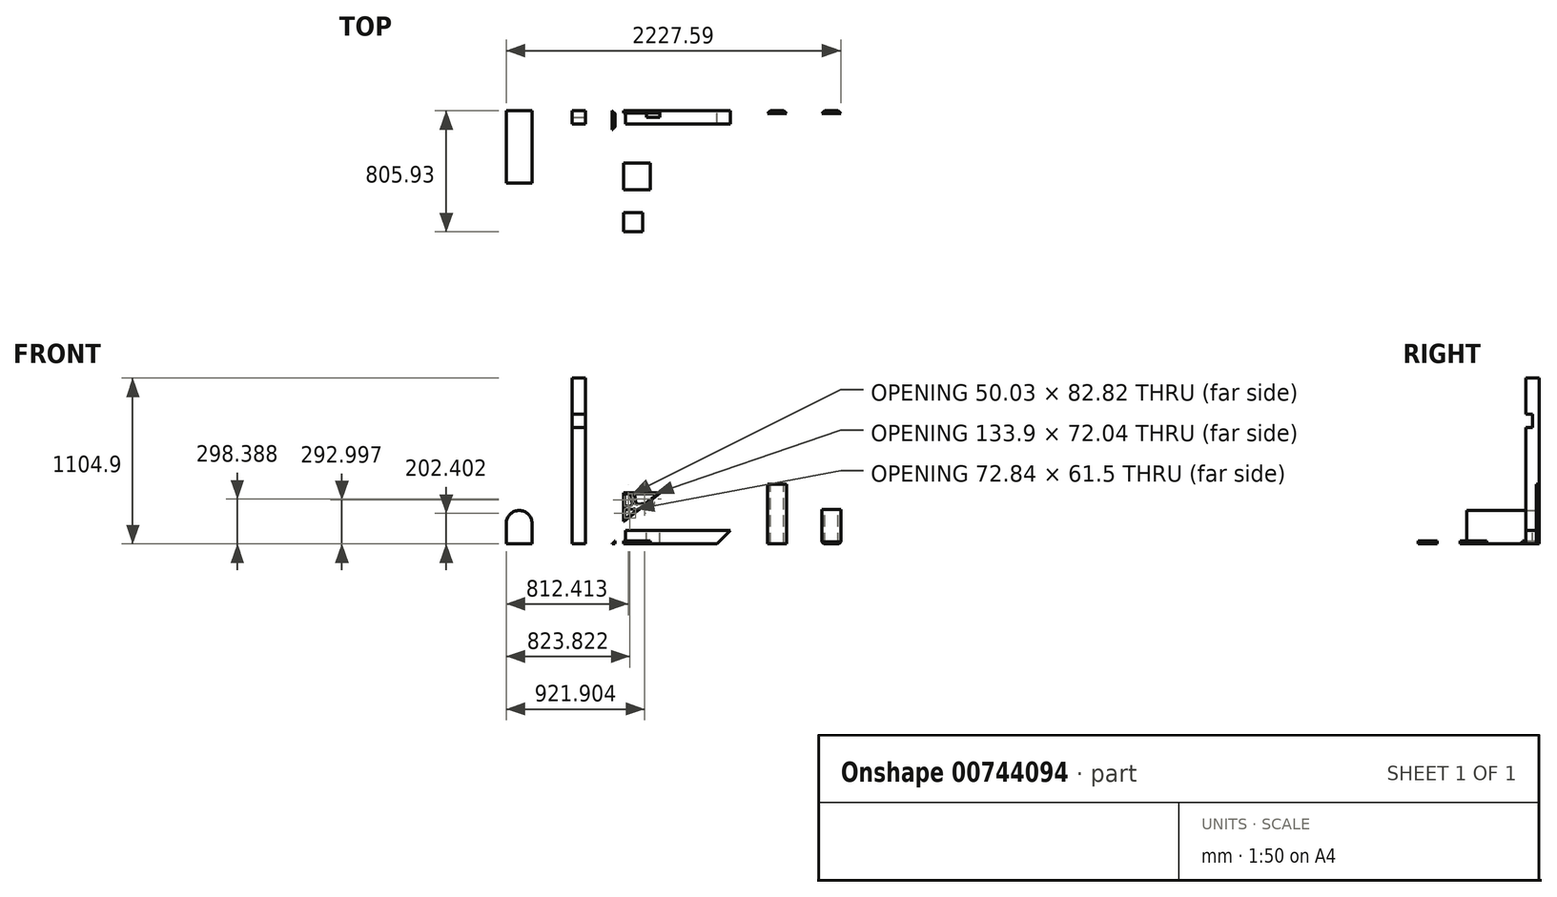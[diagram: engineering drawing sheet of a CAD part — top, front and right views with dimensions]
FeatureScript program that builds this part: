
annotation { "Feature Type Name" : "Feature", "Feature Type Description" : "" }
export const myFeature = defineFeature(function(context is Context, id is Id, definition is map)
    precondition{}
    {
        {
            var Q0;
            Q0=qCreatedBy(makeId("Front.planeOp"),FACE);
            var sketch = newSketch(context, id + "F0", { "sketchPlane" : qUnion([Q0])});
            skLineSegment(sketch, "E0", {"start": v(-781.05, 0) * mm, "end": v(-609.6, 0) * mm});
            skLineSegment(sketch, "E1", {"start": v(-781.05, 0) * mm, "end": v(-781.05, 136.53) * mm});
            skLineSegment(sketch, "E2", {"start": v(-609.6, 0) * mm, "end": v(-609.6, 136.53) * mm});
            skArc(sketch, "E3", {"start": v(-781.05, 136.53) * mm, "mid": v(-695.32, 222.25) * mm, "end": v(-609.6, 136.53) * mm});
            skSolve(sketch);
        }
        {
            var Q0;
            Q0=makeQuery(id+"F0.imprint","IMPRINT",FACE,{"disambiguationData":[TD([[makeQuery(id+"F0.imprint","IMPRINT",EDGE,{"derivedFrom":sQuery(id+"F0.wireOp",EDGE,"E0")}),1.0]])]});
            extrude(context, id + "F1", {"entities" : qUnion([Q0]), "depth" : 482.6 * mm, "offsetDistance" : 25.4 * mm});
        }
        {
            var Q0;
            Q0=qCreatedBy(makeId("Front.planeOp"),FACE);
            var sketch = newSketch(context, id + "F2", { "sketchPlane" : qUnion([Q0])});
            skLineSegment(sketch, "E4.bottom", {"start": v(-342.9, 0) * mm, "end": v(-254, 0) * mm});
            skLineSegment(sketch, "E4.left", {"start": v(-342.9, 0) * mm, "end": v(-342.9, 1104.9) * mm});
            skLineSegment(sketch, "E4.right", {"start": v(-254, 0) * mm, "end": v(-254, 1193.8) * mm});
            skLineSegment(sketch, "E5", {"start": v(-254, 1193.8) * mm, "end": v(-342.9, 1104.9) * mm});
            skSolve(sketch);
        }
        {
            var Q0;
            Q0=makeQuery(id+"F2.imprint","IMPRINT",FACE,{"disambiguationData":[TD([[makeQuery(id+"F2.imprint","IMPRINT",EDGE,{"derivedFrom":sQuery(id+"F2.wireOp",EDGE,"E4.bottom")}),1.0]])]});
            extrude(context, id + "F3", {"entities" : qUnion([Q0]), "depth" : 88.9 * mm, "offsetDistance" : 25.4 * mm});
        }
        {
            var Q0;
            Q0=makeQuery(id+"F3.opExtrude","CAP_FACE",FACE,{"disambiguationData":[OSD([sQuery(id+"F2.wireOp",EDGE,"E4.bottom"),sQuery(id+"F2.wireOp",EDGE,"E4.left"),sQuery(id+"F2.wireOp",EDGE,"E4.right"),sQuery(id+"F2.wireOp",EDGE,"E5")])],"isStart":false});
            var sketch = newSketch(context, id + "F4", { "sketchPlane" : qUnion([Q0])});
            skLineSegment(sketch, "E6.bottom", {"start": v(-342.9, 863.6) * mm, "end": v(-254, 863.6) * mm});
            skLineSegment(sketch, "E6.top", {"start": v(-342.9, 774.7) * mm, "end": v(-254, 774.7) * mm});
            skLineSegment(sketch, "E6.left", {"start": v(-342.9, 863.6) * mm, "end": v(-342.9, 774.7) * mm});
            skLineSegment(sketch, "E6.right", {"start": v(-254, 863.6) * mm, "end": v(-254, 774.7) * mm});
            skSolve(sketch);
        }
        {
            var Q0;
            Q0=makeQuery(id+"F4.imprint","IMPRINT",FACE,{"disambiguationData":[TD([[makeQuery(id+"F4.imprint","IMPRINT",EDGE,{"derivedFrom":sQuery(id+"F4.wireOp",EDGE,"E6.bottom")}),-1.0]])]});
            extrude(context, id + "F5", {"entities" : qUnion([Q0]), "operationType" : NewBodyOperationType.REMOVE, "oppositeDirection" : true, "depth" : 44.45 * mm, "offsetDistance" : 25.4 * mm});
        }
        {
            var Q0;
            Q0=qCreatedBy(makeId("Front.planeOp"),FACE);
            var sketch = newSketch(context, id + "F6", { "sketchPlane" : qUnion([Q0])});
            skLineSegment(sketch, "E7.bottom", {"start": v(-76.2, 0) * mm, "end": v(622.3, 0) * mm});
            skLineSegment(sketch, "E7.top", {"start": v(12.7, 88.9) * mm, "end": v(711.2, 88.9) * mm});
            skLineSegment(sketch, "E8", {"start": v(711.2, 88.9) * mm, "end": v(622.3, 0) * mm});
            skLineSegment(sketch, "E9", {"start": v(-76.2, 0) * mm, "end": v(12.7, 88.9) * mm});
            skSolve(sketch);
        }
        {
            var Q0;
            Q0=makeQuery(id+"F6.imprint","IMPRINT",FACE,{"disambiguationData":[TD([[makeQuery(id+"F6.imprint","IMPRINT",EDGE,{"derivedFrom":sQuery(id+"F6.wireOp",EDGE,"E7.bottom")}),1.0]])]});
            extrude(context, id + "F7", {"entities" : qUnion([Q0]), "depth" : 88.9 * mm, "offsetDistance" : 25.4 * mm});
        }
        {
            var Q0;
            Q0=makeQuery(id+"F7.opExtrude","CAP_FACE",FACE,{"disambiguationData":[OSD([sQuery(id+"F6.wireOp",EDGE,"E7.bottom"),sQuery(id+"F6.wireOp",EDGE,"E7.top"),sQuery(id+"F6.wireOp",EDGE,"E8"),sQuery(id+"F6.wireOp",EDGE,"E9")])],"isStart":true});
            var sketch = newSketch(context, id + "F8", { "sketchPlane" : qUnion([Q0])});
            skLineSegment(sketch, "E10.bottom", {"start": v(-152.4, 0) * mm, "end": v(-241.3, 0) * mm});
            skLineSegment(sketch, "E10.top", {"start": v(-152.4, 88.9) * mm, "end": v(-241.3, 88.9) * mm});
            skLineSegment(sketch, "E10.left", {"start": v(-152.4, 0) * mm, "end": v(-152.4, 88.9) * mm});
            skLineSegment(sketch, "E10.right", {"start": v(-241.3, 0) * mm, "end": v(-241.3, 88.9) * mm});
            skSolve(sketch);
        }
        {
            var Q0;
            Q0=makeQuery(id+"F8.imprint","IMPRINT",FACE,{"disambiguationData":[TD([[makeQuery(id+"F8.imprint","IMPRINT",EDGE,{"derivedFrom":sQuery(id+"F8.wireOp",EDGE,"E10.bottom")}),-1.0]])]});
            extrude(context, id + "F9", {"entities" : qUnion([Q0]), "operationType" : NewBodyOperationType.REMOVE, "oppositeDirection" : true, "depth" : 44.45 * mm, "offsetDistance" : 25.4 * mm});
        }
        {
            var Q0;
            Q0=qCreatedBy(makeId("Front.planeOp"),FACE);
            var sketch = newSketch(context, id + "F10", { "sketchPlane" : qUnion([Q0])});
            skLineSegment(sketch, "E11.bottom", {"start": v(889.1, 0) * mm, "end": v(1232, 0) * mm});
            skLineSegment(sketch, "E11.top", {"start": v(978, 88.9) * mm, "end": v(1143.1, 88.9) * mm});
            skLineSegment(sketch, "E12", {"start": v(1232, 0) * mm, "end": v(1143.1, 88.9) * mm});
            skLineSegment(sketch, "E13", {"start": v(889.1, 0) * mm, "end": v(978, 88.9) * mm});
            skSolve(sketch);
        }
        {
            var Q0;
            Q0=makeQuery(id+"F10.imprint","IMPRINT",FACE,{"disambiguationData":[TD([[makeQuery(id+"F10.imprint","IMPRINT",EDGE,{"derivedFrom":sQuery(id+"F10.wireOp",EDGE,"E11.bottom")}),1.0]])]});
            extrude(context, id + "F11", {"entities" : qUnion([Q0]), "depth" : 88.9 * mm, "offsetDistance" : 25.4 * mm});
        }
        {
            var Q0;
            {var subQ0=sQuery(id+"F2.wireOp",EDGE,"E4.left");var subQ1=sQuery(id+"F2.wireOp",EDGE,"E4.right");var subQ2=sQuery(id+"F2.wireOp",EDGE,"E5");Q0=makeQuery(id+"F5.boolean.opBoolean","SPLIT",FACE,{"disambiguationData":[TD([makeQuery(id+"F3.opExtrude","SWEPT_FACE",FACE,{"disambiguationData":[OSD([subQ2])]})])],"derivedFrom":makeQuery(id+"F3.opExtrude","CAP_FACE",FACE,{"disambiguationData":[OSD([sQuery(id+"F2.wireOp",EDGE,"E4.bottom"),subQ0,subQ1,subQ2])],"isStart":false})});}
            var sketch = newSketch(context, id + "F12", { "sketchPlane" : qUnion([Q0])});
            skLineSegment(sketch, "E14.bottom", {"start": v(-342.9, 1104.9) * mm, "end": v(-254, 1104.9) * mm});
            skLineSegment(sketch, "E14.top", {"start": v(-342.9, 1200.15) * mm, "end": v(-254, 1200.15) * mm});
            skLineSegment(sketch, "E14.left", {"start": v(-342.9, 1104.9) * mm, "end": v(-342.9, 1200.15) * mm});
            skLineSegment(sketch, "E14.right", {"start": v(-254, 1104.9) * mm, "end": v(-254, 1200.15) * mm});
            skSolve(sketch);
        }
        {
            var Q0;
            Q0 = qSketchRegion(id + "F12", true);
            extrude(context, id + "F13", {"entities" : qUnion([Q0]), "operationType" : NewBodyOperationType.REMOVE, "oppositeDirection" : true, "depth" : 88.9 * mm, "offsetDistance" : 25.4 * mm});
        }
        {
            var Q0;
            Q0=makeQuery(id+"F7.opExtrude","CAP_FACE",FACE,{"disambiguationData":[OSD([sQuery(id+"F6.wireOp",EDGE,"E7.bottom"),sQuery(id+"F6.wireOp",EDGE,"E7.top"),sQuery(id+"F6.wireOp",EDGE,"E8"),sQuery(id+"F6.wireOp",EDGE,"E9")])],"isStart":false});
            var sketch = newSketch(context, id + "F14", { "sketchPlane" : qUnion([Q0])});
            skLineSegment(sketch, "E15.bottom", {"start": v(12.7, 88.9) * mm, "end": v(-82.55, 88.9) * mm});
            skLineSegment(sketch, "E15.top", {"start": v(12.7, 0) * mm, "end": v(-82.55, 0) * mm});
            skLineSegment(sketch, "E15.left", {"start": v(12.7, 88.9) * mm, "end": v(12.7, 0) * mm});
            skLineSegment(sketch, "E15.right", {"start": v(-82.55, 88.9) * mm, "end": v(-82.55, 0) * mm});
            skSolve(sketch);
        }
        {
            var Q0;
            Q0=makeQuery(id+"F14.imprint","IMPRINT",FACE,{"disambiguationData":[TD([[makeQuery(id+"F14.imprint","IMPRINT",EDGE,{"derivedFrom":sQuery(id+"F14.wireOp",EDGE,"E15.bottom")}),1.0]])]});
            var Q1;
            {var subQ2=sQuery(id+"F14.wireOp",EDGE,"E15.left");Q1=makeQuery(id+"F14.imprint","IMPRINT",FACE,{"disambiguationData":[TD([[makeQuery(id+"F14.imprint","IMPRINT",EDGE,{"derivedFrom":subQ2}),-1.0]])]});}
            extrude(context, id + "F15", {"entities" : qUnion([Q0, Q1]), "operationType" : NewBodyOperationType.REMOVE, "oppositeDirection" : true, "depth" : 88.9 * mm, "offsetDistance" : 25.4 * mm});
        }
        {
            var Q0;
            Q0=makeQuery(id+"F11.opExtrude","SWEPT_BODY",BODY,{"disambiguationData":[OSD([sQuery(id+"F10.wireOp",EDGE,"E11.bottom"),sQuery(id+"F10.wireOp",EDGE,"E11.top"),sQuery(id+"F10.wireOp",EDGE,"E12"),sQuery(id+"F10.wireOp",EDGE,"E13")])]});
            deleteBodies(context, id + "F16", {"entities" : qUnion([Q0])});
        }
        {
            var Q0;
            Q0=qCreatedBy(makeId("Front.planeOp"),FACE);
            var sketch = newSketch(context, id + "F17", { "sketchPlane" : qUnion([Q0])});
            skLineSegment(sketch, "E16.bottom", {"start": v(959.17, 0) * mm, "end": v(1086.17, 0) * mm});
            skLineSegment(sketch, "E16.top", {"start": v(959.17, 396.88) * mm, "end": v(1086.17, 396.88) * mm});
            skLineSegment(sketch, "E16.left", {"start": v(959.17, 0) * mm, "end": v(959.17, 396.88) * mm});
            skLineSegment(sketch, "E16.right", {"start": v(1086.17, 0) * mm, "end": v(1086.17, 396.88) * mm});
            skSolve(sketch);
        }
        {
            var Q0;
            Q0=makeQuery(id+"F17.imprint","IMPRINT",FACE,{"disambiguationData":[TD([[makeQuery(id+"F17.imprint","IMPRINT",EDGE,{"derivedFrom":sQuery(id+"F17.wireOp",EDGE,"E16.bottom")}),1.0]])]});
            extrude(context, id + "F18", {"entities" : qUnion([Q0]), "depth" : 19.05 * mm, "offsetDistance" : 25.4 * mm});
        }
        {
            var Q0;
            Q0=makeQuery(id+"F18.opExtrude","SWEPT_FACE",FACE,{"disambiguationData":[OSD([sQuery(id+"F17.wireOp",EDGE,"E16.top")])]});
            var sketch = newSketch(context, id + "F19", { "sketchPlane" : qUnion([Q0])});
            skLineSegment(sketch, "E17", {"start": v(959.17, -19.05) * mm, "end": v(978.22, 0) * mm});
            skLineSegment(sketch, "E18", {"start": v(1086.17, -19.05) * mm, "end": v(1067.12, 0) * mm});
            skLineSegment(sketch, "E19", {"start": v(978.22, 0) * mm, "end": v(959.17, 0) * mm});
            skLineSegment(sketch, "E20", {"start": v(959.17, 0) * mm, "end": v(959.17, -19.05) * mm});
            skLineSegment(sketch, "E21", {"start": v(1067.12, 0) * mm, "end": v(1086.17, 0) * mm});
            skLineSegment(sketch, "E22", {"start": v(1086.17, 0) * mm, "end": v(1086.17, -19.05) * mm});
            skSolve(sketch);
        }
        {
            var Q0;
            Q0=makeQuery(id+"F19.imprint","IMPRINT",FACE,{"disambiguationData":[TD([[makeQuery(id+"F19.imprint","IMPRINT",EDGE,{"derivedFrom":sQuery(id+"F19.wireOp",EDGE,"E17")}),1.0]])]});
            var Q1;
            Q1=makeQuery(id+"F19.imprint","IMPRINT",FACE,{"disambiguationData":[TD([[makeQuery(id+"F19.imprint","IMPRINT",EDGE,{"derivedFrom":sQuery(id+"F19.wireOp",EDGE,"E18")}),-1.0]])]});
            extrude(context, id + "F20", {"entities" : qUnion([Q0, Q1]), "operationType" : NewBodyOperationType.REMOVE, "endBound" : BoundingType.THROUGH_ALL, "oppositeDirection" : true, "depth" : 25.4 * mm, "offsetDistance" : 25.4 * mm});
        }
        {
            var Q0;
            Q0=qCreatedBy(makeId("Front.planeOp"),FACE);
            var sketch = newSketch(context, id + "F21", { "sketchPlane" : qUnion([Q0])});
            skLineSegment(sketch, "E23.bottom", {"start": v(1319.54, 0) * mm, "end": v(1446.54, 0) * mm});
            skLineSegment(sketch, "E23.top", {"start": v(1319.54, 228.6) * mm, "end": v(1446.54, 228.6) * mm});
            skLineSegment(sketch, "E23.left", {"start": v(1319.54, 0) * mm, "end": v(1319.54, 228.6) * mm});
            skLineSegment(sketch, "E23.right", {"start": v(1446.54, 0) * mm, "end": v(1446.54, 228.6) * mm});
            skSolve(sketch);
        }
        {
            var Q0;
            Q0=makeQuery(id+"F21.imprint","IMPRINT",FACE,{"disambiguationData":[TD([[makeQuery(id+"F21.imprint","IMPRINT",EDGE,{"derivedFrom":sQuery(id+"F21.wireOp",EDGE,"E23.bottom")}),1.0]])]});
            extrude(context, id + "F22", {"entities" : qUnion([Q0]), "depth" : 19.05 * mm, "offsetDistance" : 25.4 * mm});
        }
        {
            var Q0;
            Q0=makeQuery(id+"F22.opExtrude","SWEPT_FACE",FACE,{"disambiguationData":[OSD([sQuery(id+"F21.wireOp",EDGE,"E23.top")])]});
            var sketch = newSketch(context, id + "F23", { "sketchPlane" : qUnion([Q0])});
            skLineSegment(sketch, "E24", {"start": v(1319.54, -19.05) * mm, "end": v(1338.6, 0) * mm});
            skLineSegment(sketch, "E25", {"start": v(1338.6, 0) * mm, "end": v(1319.54, 0) * mm});
            skLineSegment(sketch, "E26", {"start": v(1319.54, 0) * mm, "end": v(1319.54, -19.05) * mm});
            skLineSegment(sketch, "E27", {"start": v(1446.54, -19.05) * mm, "end": v(1427.5, 0) * mm});
            skLineSegment(sketch, "E28", {"start": v(1427.5, 0) * mm, "end": v(1446.54, 0) * mm});
            skLineSegment(sketch, "E29", {"start": v(1446.54, 0) * mm, "end": v(1446.54, -19.05) * mm});
            skSolve(sketch);
        }
        {
            var Q0;
            Q0=makeQuery(id+"F23.imprint","IMPRINT",FACE,{"disambiguationData":[TD([[makeQuery(id+"F23.imprint","IMPRINT",EDGE,{"derivedFrom":sQuery(id+"F23.wireOp",EDGE,"E27")}),-1.0]])]});
            var Q1;
            Q1=makeQuery(id+"F23.imprint","IMPRINT",FACE,{"disambiguationData":[TD([[makeQuery(id+"F23.imprint","IMPRINT",EDGE,{"derivedFrom":sQuery(id+"F23.wireOp",EDGE,"E24")}),1.0]])]});
            extrude(context, id + "F24", {"entities" : qUnion([Q0, Q1]), "operationType" : NewBodyOperationType.REMOVE, "endBound" : BoundingType.THROUGH_ALL, "oppositeDirection" : true, "depth" : 25.4 * mm, "offsetDistance" : 25.4 * mm});
        }
        {
            var Q0;
            Q0=qCreatedBy(makeId("Front.planeOp"),FACE);
            var sketch = newSketch(context, id + "F25", { "sketchPlane" : qUnion([Q0])});
            skLineSegment(sketch, "E30.bottom", {"start": v(-57.23, 0) * mm, "end": v(-76.28, 0) * mm});
            skLineSegment(sketch, "E30.top", {"start": v(-57.23, 19.05) * mm, "end": v(-60.4, 19.05) * mm});
            skLineSegment(sketch, "E30.left", {"start": v(-57.23, 0) * mm, "end": v(-57.23, 19.05) * mm});
            skLineSegment(sketch, "E30.right", {"start": v(-76.28, 0) * mm, "end": v(-76.28, 3.18) * mm});
            skArc(sketch, "E31", {"start": v(-76.28, 3.18) * mm, "mid": v(-65.06, 7.82) * mm, "end": v(-60.4, 19.05) * mm});
            skSolve(sketch);
        }
        {
            var Q0;
            Q0=makeQuery(id+"F25.imprint","IMPRINT",FACE,{"disambiguationData":[TD([[makeQuery(id+"F25.imprint","IMPRINT",EDGE,{"derivedFrom":sQuery(id+"F25.wireOp",EDGE,"E30.bottom")}),-1.0]])]});
            extrude(context, id + "F26", {"entities" : qUnion([Q0]), "depth" : 127 * mm, "offsetDistance" : 25.4 * mm});
        }
        {
            var Q0;
            Q0=makeQuery(id+"F26.opExtrude","SWEPT_FACE",FACE,{"disambiguationData":[OSD([sQuery(id+"F25.wireOp",EDGE,"E30.bottom")])]});
            var sketch = newSketch(context, id + "F27", { "sketchPlane" : qUnion([Q0])});
            skLineSegment(sketch, "E32", {"start": v(-76.28, 0) * mm, "end": v(-57.23, 19.05) * mm});
            skLineSegment(sketch, "E33", {"start": v(-76.28, 127) * mm, "end": v(-57.23, 107.95) * mm});
            skLineSegment(sketch, "E34", {"start": v(-57.23, 107.95) * mm, "end": v(-57.23, 127) * mm});
            skLineSegment(sketch, "E35", {"start": v(-57.23, 127) * mm, "end": v(-76.28, 127) * mm});
            skLineSegment(sketch, "E36", {"start": v(-76.28, 0) * mm, "end": v(-57.23, 0) * mm});
            skLineSegment(sketch, "E37", {"start": v(-57.23, 0) * mm, "end": v(-57.23, 19.05) * mm});
            skSolve(sketch);
        }
        {
            var Q0;
            Q0=makeQuery(id+"F27.imprint","IMPRINT",FACE,{"disambiguationData":[TD([[makeQuery(id+"F27.imprint","IMPRINT",EDGE,{"derivedFrom":sQuery(id+"F27.wireOp",EDGE,"E32")}),-1.0]])]});
            var Q1;
            Q1=makeQuery(id+"F27.imprint","IMPRINT",FACE,{"disambiguationData":[TD([[makeQuery(id+"F27.imprint","IMPRINT",EDGE,{"derivedFrom":sQuery(id+"F27.wireOp",EDGE,"E33")}),1.0]])]});
            extrude(context, id + "F28", {"entities" : qUnion([Q0, Q1]), "operationType" : NewBodyOperationType.REMOVE, "endBound" : BoundingType.THROUGH_ALL, "oppositeDirection" : true, "depth" : 25.4 * mm, "offsetDistance" : 25.4 * mm});
        }
        {
            var Q0;
            Q0=qCreatedBy(makeId("Top.planeOp"),FACE);
            var sketch = newSketch(context, id + "F29", { "sketchPlane" : qUnion([Q0])});
            skLineSegment(sketch, "E38.bottom", {"start": v(0, -525.83) * mm, "end": v(177.8, -525.83) * mm});
            skLineSegment(sketch, "E38.top", {"start": v(0, -348.03) * mm, "end": v(177.8, -348.03) * mm});
            skLineSegment(sketch, "E38.left", {"start": v(0, -525.83) * mm, "end": v(0, -348.03) * mm});
            skLineSegment(sketch, "E38.right", {"start": v(177.8, -525.83) * mm, "end": v(177.8, -348.03) * mm});
            skSolve(sketch);
        }
        {
            var Q0;
            Q0=makeQuery(id+"F29.imprint","IMPRINT",FACE,{"disambiguationData":[TD([[makeQuery(id+"F29.imprint","IMPRINT",EDGE,{"derivedFrom":sQuery(id+"F29.wireOp",EDGE,"E38.bottom")}),1.0]])]});
            extrude(context, id + "F30", {"entities" : qUnion([Q0]), "depth" : 19.05 * mm, "offsetDistance" : 25.4 * mm});
        }
        {
            var Q0;
            Q0=qCreatedBy(makeId("Top.planeOp"),FACE);
            var sketch = newSketch(context, id + "F31", { "sketchPlane" : qUnion([Q0])});
            skLineSegment(sketch, "E39.bottom", {"start": v(0, -805.93) * mm, "end": v(127, -805.93) * mm});
            skLineSegment(sketch, "E39.top", {"start": v(0, -678.93) * mm, "end": v(127, -678.93) * mm});
            skLineSegment(sketch, "E39.left", {"start": v(0, -805.93) * mm, "end": v(0, -678.93) * mm});
            skLineSegment(sketch, "E39.right", {"start": v(127, -805.93) * mm, "end": v(127, -678.93) * mm});
            skSolve(sketch);
        }
        {
            var Q0;
            Q0=makeQuery(id+"F31.imprint","IMPRINT",FACE,{"disambiguationData":[TD([[makeQuery(id+"F31.imprint","IMPRINT",EDGE,{"derivedFrom":sQuery(id+"F31.wireOp",EDGE,"E39.bottom")}),1.0]])]});
            extrude(context, id + "F32", {"entities" : qUnion([Q0]), "depth" : 19.05 * mm, "offsetDistance" : 25.4 * mm});
        }
        {
            var Q0;
            Q0=qCreatedBy(makeId("Front.planeOp"),FACE);
            var sketch = newSketch(context, id + "F33", { "sketchPlane" : qUnion([Q0])});
            skLineSegment(sketch, "E40.bottom", {"start": v(0, 150.26) * mm, "end": v(241.3, 150.26) * mm});
            skLineSegment(sketch, "E40.top", {"start": v(0, 340.76) * mm, "end": v(241.3, 340.76) * mm});
            skLineSegment(sketch, "E40.left", {"start": v(0, 150.26) * mm, "end": v(0, 340.76) * mm});
            skLineSegment(sketch, "E40.right", {"start": v(241.3, 150.26) * mm, "end": v(241.3, 340.76) * mm});
            skSolve(sketch);
        }
        {
            var Q0;
            Q0=makeQuery(id+"F33.imprint","IMPRINT",FACE,{"disambiguationData":[TD([[makeQuery(id+"F33.imprint","IMPRINT",EDGE,{"derivedFrom":sQuery(id+"F33.wireOp",EDGE,"E40.bottom")}),1.0]])]});
            extrude(context, id + "F34", {"entities" : qUnion([Q0]), "depth" : 15.88 * mm, "offsetDistance" : 25.4 * mm});
        }
        {
            var Q0;
            Q0=makeQuery(id+"F34.opExtrude","CAP_FACE",FACE,{"disambiguationData":[OSD([sQuery(id+"F33.wireOp",EDGE,"E40.bottom"),sQuery(id+"F33.wireOp",EDGE,"E40.top"),sQuery(id+"F33.wireOp",EDGE,"E40.left"),sQuery(id+"F33.wireOp",EDGE,"E40.right")])],"isStart":false});
            var sketch = newSketch(context, id + "F35", { "sketchPlane" : qUnion([Q0])});
            skLineSegment(sketch, "E41", {"start": v(3.17, 337.58) * mm, "end": v(3.18, 150.26) * mm, "construction": true});
            skLineSegment(sketch, "E42", {"start": v(3.17, 337.58) * mm, "end": v(241.3, 337.58) * mm, "construction": true});
            skLineSegment(sketch, "E43", {"start": v(3.17, 150.26) * mm, "end": v(241.3, 337.58) * mm});
            skLineSegment(sketch, "E44", {"start": v(241.3, 337.58) * mm, "end": v(241.3, 150.26) * mm});
            skLineSegment(sketch, "E45", {"start": v(241.3, 150.26) * mm, "end": v(3.17, 150.26) * mm});
            skSolve(sketch);
        }
        {
            var Q0;
            Q0=makeQuery(id+"F35.imprint","IMPRINT",FACE,{"disambiguationData":[TD([[makeQuery(id+"F35.imprint","IMPRINT",EDGE,{"derivedFrom":sQuery(id+"F35.wireOp",EDGE,"E43")}),-1.0]])]});
            extrude(context, id + "F36", {"entities" : qUnion([Q0]), "operationType" : NewBodyOperationType.REMOVE, "endBound" : BoundingType.THROUGH_ALL, "oppositeDirection" : true, "depth" : 25.4 * mm, "offsetDistance" : 25.4 * mm});
        }
        {
            var Q0;
            Q0=makeQuery(id+"F34.opExtrude","CAP_FACE",FACE,{"disambiguationData":[OSD([sQuery(id+"F33.wireOp",EDGE,"E40.bottom"),sQuery(id+"F33.wireOp",EDGE,"E40.top"),sQuery(id+"F33.wireOp",EDGE,"E40.left"),sQuery(id+"F33.wireOp",EDGE,"E40.right")])],"isStart":false});
            var sketch = newSketch(context, id + "F37", { "sketchPlane" : qUnion([Q0])});
            skLineSegment(sketch, "E46.0", {"start": v(6.35, 160.83) * mm, "end": v(6.35, 224.33) * mm});
            skLineSegment(sketch, "E46.1", {"start": v(6.35, 160.83) * mm, "end": v(105.15, 238.55) * mm});
            skLineSegment(sketch, "E46.2", {"start": v(6.35, 334.4) * mm, "end": v(46.65, 334.4) * mm});
            skLineSegment(sketch, "E47", {"start": v(6.35, 224.33) * mm, "end": v(105.15, 238.55) * mm});
            skLineSegment(sketch, "E48", {"start": v(6.35, 250) * mm, "end": v(57.74, 257.4) * mm});
            skLineSegment(sketch, "E49", {"start": v(82.88, 261.01) * mm, "end": v(72.31, 334.4) * mm});
            skLineSegment(sketch, "E50", {"start": v(57.74, 257.4) * mm, "end": v(46.65, 334.4) * mm});
            skLineSegment(sketch, "E51.trimOffspring", {"start": v(72.31, 334.4) * mm, "end": v(227, 334.4) * mm});
            skLineSegment(sketch, "E52.trimOffspring", {"start": v(82.88, 261.01) * mm, "end": v(145.07, 269.96) * mm});
            skLineSegment(sketch, "E53.trimOffspring", {"start": v(145.07, 269.96) * mm, "end": v(227, 334.4) * mm});
            skLineSegment(sketch, "E54.trimOffspring", {"start": v(6.35, 250) * mm, "end": v(6.35, 334.4) * mm});
            skSolve(sketch);
        }
        {
            var Q0;
            Q0=makeQuery(id+"F37.imprint","IMPRINT",FACE,{"disambiguationData":[TD([[makeQuery(id+"F37.imprint","IMPRINT",EDGE,{"derivedFrom":sQuery(id+"F37.wireOp",EDGE,"E46.0")}),-1.0]])]});
            var Q1;
            Q1=makeQuery(id+"F37.imprint","IMPRINT",FACE,{"disambiguationData":[TD([[makeQuery(id+"F37.imprint","IMPRINT",EDGE,{"derivedFrom":sQuery(id+"F37.wireOp",EDGE,"E46.2")}),-1.0]])]});
            var Q2;
            Q2=makeQuery(id+"F37.imprint","IMPRINT",FACE,{"disambiguationData":[TD([[makeQuery(id+"F37.imprint","IMPRINT",EDGE,{"derivedFrom":sQuery(id+"F37.wireOp",EDGE,"E49")}),-1.0]])]});
            extrude(context, id + "F38", {"entities" : qUnion([Q0, Q1, Q2]), "operationType" : NewBodyOperationType.REMOVE, "endBound" : BoundingType.THROUGH_ALL, "oppositeDirection" : true, "depth" : 25.4 * mm, "offsetDistance" : 25.4 * mm});
        }
        {
            var Q0;
            Q0=makeQuery(id+"F38.boolean.opBoolean","COPY",EDGE,{"derivedFrom":makeQuery(id+"F38.opExtrude","SWEPT_EDGE",EDGE,{"disambiguationData":[OSD([sQuery(id+"F37.wireOp",EDGE,"E52.trimOffspring"),sQuery(id+"F37.wireOp",EDGE,"E53.trimOffspring")])]})});
            var Q1;
            Q1=makeQuery(id+"F38.boolean.opBoolean","COPY",EDGE,{"derivedFrom":makeQuery(id+"F38.opExtrude","SWEPT_EDGE",EDGE,{"disambiguationData":[OSD([sQuery(id+"F37.wireOp",EDGE,"E49"),sQuery(id+"F37.wireOp",EDGE,"E52.trimOffspring")])]})});
            var Q2;
            Q2=makeQuery(id+"F38.boolean.opBoolean","COPY",EDGE,{"derivedFrom":makeQuery(id+"F38.opExtrude","SWEPT_EDGE",EDGE,{"disambiguationData":[OSD([sQuery(id+"F37.wireOp",EDGE,"E49"),sQuery(id+"F37.wireOp",EDGE,"E51.trimOffspring")])]})});
            var Q3;
            Q3=makeQuery(id+"F38.boolean.opBoolean","COPY",EDGE,{"derivedFrom":makeQuery(id+"F38.opExtrude","SWEPT_EDGE",EDGE,{"disambiguationData":[OSD([sQuery(id+"F37.wireOp",EDGE,"E51.trimOffspring"),sQuery(id+"F37.wireOp",EDGE,"E53.trimOffspring")])]})});
            var Q4;
            Q4=makeQuery(id+"F38.boolean.opBoolean","COPY",EDGE,{"derivedFrom":makeQuery(id+"F38.opExtrude","SWEPT_EDGE",EDGE,{"disambiguationData":[OSD([sQuery(id+"F37.wireOp",EDGE,"E46.2"),sQuery(id+"F37.wireOp",EDGE,"E50")])]})});
            var Q5;
            Q5=makeQuery(id+"F38.boolean.opBoolean","COPY",EDGE,{"derivedFrom":makeQuery(id+"F38.opExtrude","SWEPT_EDGE",EDGE,{"disambiguationData":[OSD([sQuery(id+"F37.wireOp",EDGE,"E46.2"),sQuery(id+"F37.wireOp",EDGE,"E54.trimOffspring")])]})});
            var Q6;
            Q6=makeQuery(id+"F38.boolean.opBoolean","COPY",EDGE,{"derivedFrom":makeQuery(id+"F38.opExtrude","SWEPT_EDGE",EDGE,{"disambiguationData":[OSD([sQuery(id+"F37.wireOp",EDGE,"E48"),sQuery(id+"F37.wireOp",EDGE,"E54.trimOffspring")])]})});
            var Q7;
            Q7=makeQuery(id+"F38.boolean.opBoolean","COPY",EDGE,{"derivedFrom":makeQuery(id+"F38.opExtrude","SWEPT_EDGE",EDGE,{"disambiguationData":[OSD([sQuery(id+"F37.wireOp",EDGE,"E48"),sQuery(id+"F37.wireOp",EDGE,"E50")])]})});
            var Q8;
            Q8=makeQuery(id+"F38.boolean.opBoolean","COPY",EDGE,{"derivedFrom":makeQuery(id+"F38.opExtrude","SWEPT_EDGE",EDGE,{"disambiguationData":[OSD([sQuery(id+"F37.wireOp",EDGE,"E46.1"),sQuery(id+"F37.wireOp",EDGE,"E47")])]})});
            var Q9;
            Q9=makeQuery(id+"F38.boolean.opBoolean","COPY",EDGE,{"derivedFrom":makeQuery(id+"F38.opExtrude","SWEPT_EDGE",EDGE,{"disambiguationData":[OSD([sQuery(id+"F37.wireOp",EDGE,"E46.0"),sQuery(id+"F37.wireOp",EDGE,"E47")])]})});
            var Q10;
            Q10=makeQuery(id+"F38.boolean.opBoolean","COPY",EDGE,{"derivedFrom":makeQuery(id+"F38.opExtrude","SWEPT_EDGE",EDGE,{"disambiguationData":[OSD([sQuery(id+"F37.wireOp",EDGE,"E46.0"),sQuery(id+"F37.wireOp",EDGE,"E46.1")])]})});
            fillet(context, id + "F39", {"entities" : qUnion([Q0, Q1, Q2, Q3, Q4, Q5, Q6, Q7, Q8, Q9, Q10]), "radius" : 10.16 * mm, "tangentPropagation" : true, "allowEdgeOverflow" : false});
        }
        {
            var Q0;
            Q0=makeQuery(id+"F22.opExtrude","CAP_EDGE",EDGE,{"disambiguationData":[OSD([sQuery(id+"F21.wireOp",EDGE,"E23.bottom")])],"isStart":false});
            chamfer(context, id + "F40", {"entities" : qUnion([Q0]), "width" : 12.7 * mm, "tangentPropagation" : true});
        }
    });
